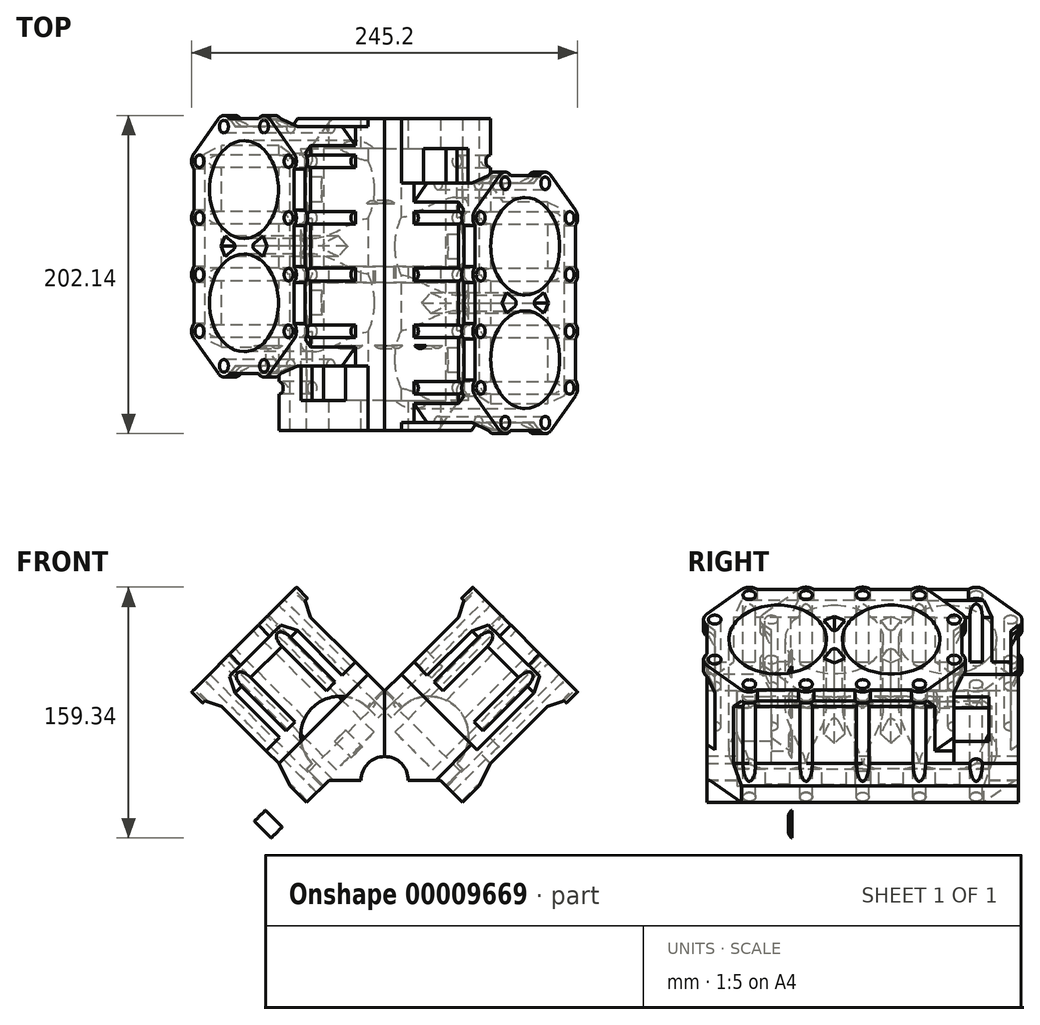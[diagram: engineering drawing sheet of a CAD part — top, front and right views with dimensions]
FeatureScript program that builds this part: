
annotation { "Feature Type Name" : "Feature", "Feature Type Description" : "" }
export const myFeature = defineFeature(function(context is Context, id is Id, definition is map)
    precondition{}
    {
        {
            var Q0;
            Q0=qCreatedBy(makeId("Front.planeOp"),FACE);
            var sketch = newSketch(context, id + "F0", { "sketchPlane" : qUnion([Q0]), "disableImprinting" : false});
            skLineSegment(sketch, "E0", {"start": v(0, 0) * mm, "end": v(-89.32, 89.32) * mm, "construction": true});
            skLineSegment(sketch, "E1", {"start": v(-89.32, 89.32) * mm, "end": v(-61.03, 117.6) * mm});
            skLineSegment(sketch, "E2", {"start": v(-89.32, 89.32) * mm, "end": v(-117.6, 61.03) * mm});
            skArc(sketch, "E3", {"start": v(-10.6, 45.96) * mm, "mid": v(-45.96, 45.96) * mm, "end": v(-45.96, 10.6) * mm});
            skLineSegment(sketch, "E4", {"start": v(0, 15) * mm, "end": v(0, 56.57) * mm});
            skArc(sketch, "E5", {"start": v(0, 15) * mm, "mid": v(-10.6, 10.6) * mm, "end": v(-15, 0) * mm});
            skLineSegment(sketch, "E6", {"start": v(-28.28, 28.28) * mm, "end": v(-10.6, 10.6) * mm});
            skLineSegment(sketch, "E7", {"start": v(0, 56.57) * mm, "end": v(-56.57, 0) * mm});
            skLineSegment(sketch, "E8", {"start": v(-15, 0) * mm, "end": v(-35.36, 0) * mm});
            skLineSegment(sketch, "E9", {"start": v(-56.57, 0) * mm, "end": v(-56.57, 0) * mm});
            skPoint(sketch, "E10", {"position": v(-56.57, 0) * mm});
            skLineSegment(sketch, "E11", {"start": v(-49.5, 7.07) * mm, "end": v(-38.9, -3.54) * mm});
            skLineSegment(sketch, "E12", {"start": v(-48.08, 5.66) * mm, "end": v(-5.61, 48.04) * mm});
            skLineSegment(sketch, "E13", {"start": v(-35.36, 0) * mm, "end": v(-49.5, -14.14) * mm});
            skLineSegment(sketch, "E14", {"start": v(-49.5, -14.14) * mm, "end": v(-60.1, -3.54) * mm});
            skLineSegment(sketch, "E15", {"start": v(-60.1, -3.54) * mm, "end": v(-56.57, 0) * mm});
            skLineSegment(sketch, "E16", {"start": v(-60.1, -3.54) * mm, "end": v(-67.18, 10.6) * mm});
            skLineSegment(sketch, "E17", {"start": v(-7.07, 49.5) * mm, "end": v(-5.61, 48.04) * mm});
            skLineSegment(sketch, "E18", {"start": v(-117.6, 61.03) * mm, "end": v(-121.14, 57.5) * mm});
            skLineSegment(sketch, "E19", {"start": v(-121.14, 57.5) * mm, "end": v(-114.07, 50.43) * mm});
            skLineSegment(sketch, "E20", {"start": v(-114.07, 50.43) * mm, "end": v(-103.46, 46.89) * mm});
            skLineSegment(sketch, "E21", {"start": v(-67.18, 10.6) * mm, "end": v(-103.46, 46.89) * mm});
            skLineSegment(sketch, "E22", {"start": v(-61.03, 117.6) * mm, "end": v(-57.5, 121.14) * mm});
            skLineSegment(sketch, "E23", {"start": v(-57.5, 121.14) * mm, "end": v(-50.43, 114.07) * mm});
            skLineSegment(sketch, "E24", {"start": v(-50.43, 114.07) * mm, "end": v(-46.89, 103.46) * mm});
            skLineSegment(sketch, "E25", {"start": v(-46.89, 103.46) * mm, "end": v(0, 56.57) * mm});
            skSolve(sketch);
        }
        {
            var Q0;
            Q0=makeQuery(id+"F0.imprint","IMPRINT",FACE,{"disambiguationData":[TD([[makeQuery(id+"F0.imprint","IMPRINT",EDGE,{"derivedFrom":sQuery(id+"F0.wireOp",EDGE,"E1")}),-1.0]])]});
            var Q1;
            {var subQ6=sQuery(id+"F0.wireOp",EDGE,"7077ad60-6c45-4a02-82f9-83b4f3b2e26d");Q1=makeQuery(id+"F0.imprint","IMPRINT",FACE,{"disambiguationData":[TD([[makeQuery(id+"F0.imprint","IMPRINT",EDGE,{"derivedFrom":subQ6}),1.0]])]});}
            var Q2;
            {var subQ5=sQuery(id+"F0.wireOp",EDGE,"00a5af6f-d9c4-4420-bd82-b76ba807b053");Q2=makeQuery(id+"F0.imprint","IMPRINT",FACE,{"disambiguationData":[TD([[makeQuery(id+"F0.imprint","IMPRINT",EDGE,{"derivedFrom":subQ5}),1.0]])]});}
            var Q3;
            {var subQ1=sQuery(id+"F0.wireOp",EDGE,"63562ab9-0a50-4102-b09f-f67702f7469f");Q3=makeQuery(id+"F0.imprint","IMPRINT",FACE,{"disambiguationData":[TD([[makeQuery(id+"F0.imprint","IMPRINT",EDGE,{"derivedFrom":subQ1}),1.0]])]});}
            var Q4;
            {var subQ3=sQuery(id+"F0.wireOp",EDGE,"E4");Q4=makeQuery(id+"F0.imprint","IMPRINT",FACE,{"disambiguationData":[TD([[makeQuery(id+"F0.imprint","IMPRINT",EDGE,{"derivedFrom":subQ3}),1.0]])]});}
            var Q5;
            Q5=makeQuery(id+"F0.imprint","IMPRINT",FACE,{"disambiguationData":[TD([[makeQuery(id+"F0.imprint","IMPRINT",EDGE,{"derivedFrom":sQuery(id+"F0.wireOp",EDGE,"61e63e8b-020c-431c-80ea-b96c9f9e3d8e")}),-1.0]])]});
            var Q6;
            {var subQ1=sQuery(id+"F0.wireOp",EDGE,"d73f1ee5-fcce-4fad-9c2f-5dffc275b150");Q6=makeQuery(id+"F0.imprint","IMPRINT",FACE,{"disambiguationData":[TD([[makeQuery(id+"F0.imprint","IMPRINT",EDGE,{"derivedFrom":subQ1}),-1.0]])]});}
            var Q7;
            {var subQ2=sQuery(id+"F0.wireOp",EDGE,"E3");Q7=makeQuery(id+"F0.imprint","IMPRINT",FACE,{"disambiguationData":[TD([[makeQuery(id+"F0.imprint","IMPRINT",EDGE,{"derivedFrom":subQ2}),1.0]])]});}
            var Q8;
            {var subQ0=sQuery(id+"F0.wireOp",EDGE,"E7");var subQ4=sQuery(id+"F0.wireOp",EDGE,"E6");var subQ5=makeQuery(id+"F0.imprint","INTERSECT",VERTEX,{"derivedFrom":[subQ4,subQ0]});Q8=makeQuery(id+"F0.imprint","IMPRINT",FACE,{"disambiguationData":[TD([[makeQuery(id+"F0.imprint","IMPRINT",EDGE,{"disambiguationData":[TD([[subQ5,-1.0]])],"derivedFrom":subQ4}),-1.0]])]});}
            var Q9;
            {var subQ0=sQuery(id+"F0.wireOp",EDGE,"E7");var subQ4=sQuery(id+"F0.wireOp",EDGE,"E6");var subQ6=makeQuery(id+"F0.imprint","INTERSECT",VERTEX,{"derivedFrom":[subQ4,subQ0]});Q9=makeQuery(id+"F0.imprint","IMPRINT",FACE,{"disambiguationData":[TD([[makeQuery(id+"F0.imprint","IMPRINT",EDGE,{"disambiguationData":[TD([[subQ6,-1.0]])],"derivedFrom":subQ4}),1.0]])]});}
            var Q10;
            {var subQ1=sQuery(id+"F0.wireOp",EDGE,"d5e2b67f-3f92-4c55-8c7c-6b2c5aceb9cd");Q10=makeQuery(id+"F0.imprint","IMPRINT",FACE,{"disambiguationData":[TD([[makeQuery(id+"F0.imprint","IMPRINT",EDGE,{"derivedFrom":subQ1}),-1.0]])]});}
            var Q11;
            {var subQ3=sQuery(id+"F0.wireOp",EDGE,"E8");Q11=makeQuery(id+"F0.imprint","IMPRINT",FACE,{"disambiguationData":[TD([[makeQuery(id+"F0.imprint","IMPRINT",EDGE,{"derivedFrom":subQ3}),-1.0]])]});}
            var Q12;
            {var subQ1=sQuery(id+"F0.wireOp",EDGE,"7da52aa7-5538-4868-8c85-49046fa19762");Q12=makeQuery(id+"F0.imprint","IMPRINT",FACE,{"disambiguationData":[TD([[makeQuery(id+"F0.imprint","IMPRINT",EDGE,{"derivedFrom":subQ1}),1.0]])]});}
            var Q13;
            {var subQ1=sQuery(id+"F0.wireOp",EDGE,"E15");Q13=makeQuery(id+"F0.imprint","IMPRINT",FACE,{"disambiguationData":[TD([[makeQuery(id+"F0.imprint","IMPRINT",EDGE,{"derivedFrom":subQ1}),1.0]])]});}
            var Q14;
            {var subQ0=sQuery(id+"F0.wireOp",EDGE,"E14");Q14=makeQuery(id+"F0.imprint","IMPRINT",FACE,{"disambiguationData":[TD([[makeQuery(id+"F0.imprint","IMPRINT",EDGE,{"derivedFrom":subQ0}),-1.0]])]});}
            extrude(context, id + "F1", {"entities" : qUnion([Q0, Q1, Q2, Q3, Q4, Q5, Q6, Q7, Q8, Q9, Q10, Q11, Q12, Q13, Q14]), "depth" : 198 * mm, "symmetric" : true});
        }
        {
            var Q0;
            {var subQ3=sQuery(id+"F0.wireOp",EDGE,"E4");Q0=makeQuery(id+"F0.imprint","IMPRINT",FACE,{"disambiguationData":[TD([[makeQuery(id+"F0.imprint","IMPRINT",EDGE,{"derivedFrom":subQ3}),1.0]])]});}
            var Q1;
            {var subQ0=sQuery(id+"F0.wireOp",EDGE,"E7");var subQ1=sQuery(id+"F0.wireOp",EDGE,"E6");var subQ2=makeQuery(id+"F0.imprint","INTERSECT",VERTEX,{"derivedFrom":[subQ1,subQ0]});Q1=makeQuery(id+"F0.imprint","IMPRINT",FACE,{"disambiguationData":[TD([[makeQuery(id+"F0.imprint","IMPRINT",EDGE,{"disambiguationData":[TD([[subQ2,-1.0]])],"derivedFrom":subQ1}),1.0]])]});}
            var Q2;
            {var subQ0=sQuery(id+"F0.wireOp",EDGE,"E7");var subQ4=sQuery(id+"F0.wireOp",EDGE,"E6");var subQ6=makeQuery(id+"F0.imprint","INTERSECT",VERTEX,{"derivedFrom":[subQ4,subQ0]});Q2=makeQuery(id+"F0.imprint","IMPRINT",FACE,{"disambiguationData":[TD([[makeQuery(id+"F0.imprint","IMPRINT",EDGE,{"disambiguationData":[TD([[subQ6,-1.0]])],"derivedFrom":subQ4}),-1.0]])]});}
            var Q3;
            {var subQ2=sQuery(id+"F0.wireOp",EDGE,"E3");Q3=makeQuery(id+"F0.imprint","IMPRINT",FACE,{"disambiguationData":[TD([[makeQuery(id+"F0.imprint","IMPRINT",EDGE,{"derivedFrom":subQ2}),1.0]])]});}
            var Q4;
            {var subQ2=sQuery(id+"F0.wireOp",EDGE,"E8");Q4=makeQuery(id+"F0.imprint","IMPRINT",FACE,{"disambiguationData":[TD([[makeQuery(id+"F0.imprint","IMPRINT",EDGE,{"derivedFrom":subQ2}),-1.0]])]});}
            extrude(context, id + "F2", {"entities" : qUnion([Q0, Q1, Q2, Q3, Q4]), "operationType" : NewBodyOperationType.REMOVE, "oppositeDirection" : true, "depth" : 160 * mm, "symmetric" : true});
        }
        {
            var Q0;
            Q0=makeQuery(id+"F1.opExtrude","SWEPT_FACE",FACE,{"disambiguationData":[OSD([sQuery(id+"F0.wireOp",EDGE,"E1"),sQuery(id+"F0.wireOp",EDGE,"E2")])]});
            var sketch = newSketch(context, id + "F3", { "sketchPlane" : qUnion([Q0])});
            skArc(sketch, "E26", {"start": v(-20.17, 9.4) * mm, "mid": v(-18, 8.15) * mm, "end": v(-15.83, 9.4) * mm});
            skLineSegment(sketch, "E27", {"start": v(-20.17, 9.4) * mm, "end": v(-24.56, 17) * mm});
            skLineSegment(sketch, "E28", {"start": v(-15.83, 9.4) * mm, "end": v(-11.44, 17) * mm});
            skLineSegment(sketch, "E29", {"start": v(-11.44, -17) * mm, "end": v(-15.83, -9.4) * mm});
            skLineSegment(sketch, "E30", {"start": v(-20.17, -9.4) * mm, "end": v(-24.56, -17) * mm});
            skArc(sketch, "E31", {"start": v(-15.83, -9.4) * mm, "mid": v(-18, -8.15) * mm, "end": v(-20.17, -9.4) * mm});
            skLineSegment(sketch, "E32", {"start": v(-11.44, 17) * mm, "end": v(-18, 20.78) * mm});
            skLineSegment(sketch, "E33", {"start": v(-18, 20.78) * mm, "end": v(-24.56, 17) * mm});
            skLineSegment(sketch, "E34", {"start": v(-24.56, -17) * mm, "end": v(-18, -20.78) * mm});
            skLineSegment(sketch, "E35", {"start": v(-18, -20.78) * mm, "end": v(-11.44, -17) * mm});
            skCircle(sketch, "E36", {"center": v(-54, 0) * mm, "radius": 31 * mm});
            skCircle(sketch, "E37", {"center": v(18, 0) * mm, "radius": 31 * mm});
            skLineSegment(sketch, "E38", {"start": v(18, 0) * mm, "end": v(-11.44, 17) * mm, "construction": true});
            skLineSegment(sketch, "E39", {"start": v(-11.44, -17) * mm, "end": v(18, 0) * mm, "construction": true});
            skLineSegment(sketch, "E40", {"start": v(-18, -20.78) * mm, "end": v(-18, 20.78) * mm, "construction": true});
            skCircle(sketch, "E41", {"center": v(-72, -40) * mm, "radius": 4 * mm});
            skCircle(sketch, "E42", {"center": v(-36, -40) * mm, "radius": 4 * mm});
            skCircle(sketch, "E43", {"center": v(0, -40) * mm, "radius": 4 * mm});
            skCircle(sketch, "E44", {"center": v(36, -40.01) * mm, "radius": 4 * mm});
            skCircle(sketch, "E45", {"center": v(36, 40.01) * mm, "radius": 4 * mm});
            skCircle(sketch, "E46", {"center": v(0, 40) * mm, "radius": 4 * mm});
            skCircle(sketch, "E47", {"center": v(-36, 40) * mm, "radius": 4 * mm});
            skCircle(sketch, "E48", {"center": v(-72, 40) * mm, "radius": 4 * mm});
            skCircle(sketch, "E49", {"center": v(-94, 18) * mm, "radius": 4 * mm});
            skCircle(sketch, "E50", {"center": v(-94, -18) * mm, "radius": 4 * mm});
            skCircle(sketch, "E51", {"center": v(58, 18) * mm, "radius": 4 * mm});
            skCircle(sketch, "E52", {"center": v(58, -18) * mm, "radius": 4 * mm});
            skCircle(sketch, "E53", {"center": v(72, -40) * mm, "radius": 4 * mm});
            skSolve(sketch);
        }
        {
            var Q0;
            {var subQ1=sQuery(id+"F3.wireOp",EDGE,"E37");var subQ3=sQuery(id+"F3.wireOp",EDGE,"ba8a5dc3-78c3-42ff-b71d-fa66224fb622");var subQ5=makeQuery(id+"F3.imprint","INTERSECT",VERTEX,{"derivedFrom":[subQ1,subQ3]});Q0=makeQuery(id+"F3.imprint","IMPRINT",FACE,{"disambiguationData":[TD([[makeQuery(id+"F3.imprint","IMPRINT",EDGE,{"disambiguationData":[TD([[subQ5,-1.0]])],"derivedFrom":subQ1}),1.0]])]});}
            var Q1;
            Q1=makeQuery(id+"F3.imprint","IMPRINT",FACE,{"disambiguationData":[TD([[makeQuery(id+"F3.imprint","IMPRINT",EDGE,{"derivedFrom":sQuery(id+"F3.wireOp",EDGE,"E36")}),1.0]])]});
            var Q2;
            Q2=makeQuery(id+"F3.imprint","IMPRINT",FACE,{"disambiguationData":[TD([[makeQuery(id+"F3.imprint","IMPRINT",EDGE,{"derivedFrom":sQuery(id+"F3.wireOp",EDGE,"E37")}),1.0]])]});
            var Q3;
            Q3=makeQuery(id+"F3.imprint","IMPRINT",FACE,{"disambiguationData":[TD([[makeQuery(id+"F3.imprint","IMPRINT",EDGE,{"derivedFrom":sQuery(id+"F3.wireOp",EDGE,"E29")}),1.0]])]});
            var Q4;
            Q4=makeQuery(id+"F3.imprint","IMPRINT",FACE,{"disambiguationData":[TD([[makeQuery(id+"F3.imprint","IMPRINT",EDGE,{"derivedFrom":sQuery(id+"F3.wireOp",EDGE,"E26")}),1.0]])]});
            extrude(context, id + "F4", {"entities" : qUnion([Q0, Q1, Q2, Q3, Q4]), "operationType" : NewBodyOperationType.REMOVE, "flatOperationType" : FlatOperationType.REMOVE, "oppositeDirection" : true, "depth" : 100 * mm, "offsetDistance" : 25 * mm, "domain" : OperationDomain.MODEL});
        }
        {
            var Q0;
            {var subQ0=sQuery(id+"F0.wireOp",EDGE,"E13");Q0=makeQuery(id+"F7.boolean.opBoolean","MERGE",FACE,{"derivedFrom":[makeQuery(id+"F1.opExtrude","SWEPT_FACE",FACE,{"disambiguationData":[OSD([subQ0])]}),makeQuery(id+"F7.opExtrude","SWEPT_FACE",FACE,{"disambiguationData":[OSD([subQ0])]})]});}
            var sketch = newSketch(context, id + "F5", { "sketchPlane" : qUnion([Q0])});
            skArc(sketch, "E54", {"start": v(-45, -66.95) * mm, "mid": v(-47.07, -71.95) * mm, "end": v(-45, -76.95) * mm});
            skArc(sketch, "E55", {"start": v(-45, -31) * mm, "mid": v(-47.07, -36) * mm, "end": v(-45, -41) * mm});
            skArc(sketch, "E56", {"start": v(-45, 5) * mm, "mid": v(-47.07, 0) * mm, "end": v(-45, -5) * mm});
            skArc(sketch, "E57", {"start": v(-45, 41) * mm, "mid": v(-47.07, 36) * mm, "end": v(-45, 31) * mm});
            skArc(sketch, "E58", {"start": v(-45, 77) * mm, "mid": v(-47.07, 72) * mm, "end": v(-45, 67) * mm});
            skLineSegment(sketch, "E59", {"start": v(-45, -76.95) * mm, "end": v(-45, -66.95) * mm});
            skLineSegment(sketch, "E60", {"start": v(-45, -41) * mm, "end": v(-45, -31) * mm});
            skLineSegment(sketch, "E61", {"start": v(-45, -5) * mm, "end": v(-45, 5) * mm});
            skLineSegment(sketch, "E62", {"start": v(-45, 67) * mm, "end": v(-45, 77) * mm});
            skLineSegment(sketch, "E63", {"start": v(-45, 41) * mm, "end": v(-45, 31) * mm});
            skSolve(sketch);
        }
        {
            var Q0;
            Q0=makeQuery(id+"F5.imprint","IMPRINT",FACE,{"disambiguationData":[TD([[makeQuery(id+"F5.imprint","IMPRINT",EDGE,{"derivedFrom":sQuery(id+"F5.wireOp",EDGE,"E54")}),1.0]])]});
            var Q1;
            Q1=makeQuery(id+"F5.imprint","IMPRINT",FACE,{"disambiguationData":[TD([[makeQuery(id+"F5.imprint","IMPRINT",EDGE,{"derivedFrom":sQuery(id+"F5.wireOp",EDGE,"E55")}),1.0]])]});
            var Q2;
            Q2=makeQuery(id+"F5.imprint","IMPRINT",FACE,{"disambiguationData":[TD([[makeQuery(id+"F5.imprint","IMPRINT",EDGE,{"derivedFrom":sQuery(id+"F5.wireOp",EDGE,"E56")}),1.0]])]});
            var Q3;
            Q3=makeQuery(id+"F5.imprint","IMPRINT",FACE,{"disambiguationData":[TD([[makeQuery(id+"F5.imprint","IMPRINT",EDGE,{"derivedFrom":sQuery(id+"F5.wireOp",EDGE,"E57")}),1.0]])]});
            var Q4;
            Q4=makeQuery(id+"F5.imprint","IMPRINT",FACE,{"disambiguationData":[TD([[makeQuery(id+"F5.imprint","IMPRINT",EDGE,{"derivedFrom":sQuery(id+"F5.wireOp",EDGE,"E58")}),1.0]])]});
            extrude(context, id + "F6", {"entities" : qUnion([Q0, Q1, Q2, Q3, Q4]), "operationType" : NewBodyOperationType.ADD, "oppositeDirection" : true, "depth" : 15 * mm});
        }
        {
            var Q0;
            {var subQ3=sQuery(id+"F0.wireOp",EDGE,"E4");Q0=makeQuery(id+"F0.imprint","IMPRINT",FACE,{"disambiguationData":[TD([[makeQuery(id+"F0.imprint","IMPRINT",EDGE,{"derivedFrom":subQ3}),1.0]])]});}
            var Q1;
            {var subQ3=sQuery(id+"F0.wireOp",EDGE,"E8");Q1=makeQuery(id+"F0.imprint","IMPRINT",FACE,{"disambiguationData":[TD([[makeQuery(id+"F0.imprint","IMPRINT",EDGE,{"derivedFrom":subQ3}),-1.0]])]});}
            var Q2;
            {var subQ1=sQuery(id+"F0.wireOp",EDGE,"7da52aa7-5538-4868-8c85-49046fa19762");Q2=makeQuery(id+"F0.imprint","IMPRINT",FACE,{"disambiguationData":[TD([[makeQuery(id+"F0.imprint","IMPRINT",EDGE,{"derivedFrom":subQ1}),1.0]])]});}
            extrude(context, id + "F7", {"entities" : qUnion([Q0, Q1, Q2]), "operationType" : NewBodyOperationType.ADD, "depth" : 10 * mm, "symmetric" : true});
        }
        {
            var Q0;
            Q0=makeQuery(id+"F3.imprint","IMPRINT",FACE,{"disambiguationData":[TD([[makeQuery(id+"F3.imprint","IMPRINT",EDGE,{"derivedFrom":sQuery(id+"F3.wireOp",EDGE,"E41")}),1.0]])]});
            var Q1;
            Q1=makeQuery(id+"F3.imprint","IMPRINT",FACE,{"disambiguationData":[TD([[makeQuery(id+"F3.imprint","IMPRINT",EDGE,{"derivedFrom":sQuery(id+"F3.wireOp",EDGE,"E42")}),1.0]])]});
            var Q2;
            Q2=makeQuery(id+"F3.imprint","IMPRINT",FACE,{"disambiguationData":[TD([[makeQuery(id+"F3.imprint","IMPRINT",EDGE,{"derivedFrom":sQuery(id+"F3.wireOp",EDGE,"E43")}),1.0]])]});
            var Q3;
            Q3=makeQuery(id+"F3.imprint","IMPRINT",FACE,{"disambiguationData":[TD([[makeQuery(id+"F3.imprint","IMPRINT",EDGE,{"derivedFrom":sQuery(id+"F3.wireOp",EDGE,"E44")}),1.0]])]});
            var Q4;
            Q4=makeQuery(id+"F3.imprint","IMPRINT",FACE,{"disambiguationData":[TD([[makeQuery(id+"F3.imprint","IMPRINT",EDGE,{"derivedFrom":sQuery(id+"F3.wireOp",EDGE,"E53")}),1.0]])]});
            extrude(context, id + "F8", {"entities" : qUnion([Q0, Q1, Q2, Q3, Q4]), "operationType" : NewBodyOperationType.REMOVE, "oppositeDirection" : true, "depth" : 110 * mm});
        }
        {
            var Q0;
            Q0=makeQuery(id+"F1.opExtrude","CAP_FACE",FACE,{"disambiguationData":[OSD([sQuery(id+"F0.wireOp",EDGE,"E1"),sQuery(id+"F0.wireOp",EDGE,"E2"),sQuery(id+"F0.wireOp",EDGE,"E4"),sQuery(id+"F0.wireOp",EDGE,"E5"),sQuery(id+"F0.wireOp",EDGE,"E8"),sQuery(id+"F0.wireOp",EDGE,"E13"),sQuery(id+"F0.wireOp",EDGE,"E14"),sQuery(id+"F0.wireOp",EDGE,"E16"),sQuery(id+"F0.wireOp",EDGE,"E18"),sQuery(id+"F0.wireOp",EDGE,"E19"),sQuery(id+"F0.wireOp",EDGE,"E20"),sQuery(id+"F0.wireOp",EDGE,"E21"),sQuery(id+"F0.wireOp",EDGE,"E22"),sQuery(id+"F0.wireOp",EDGE,"E23"),sQuery(id+"F0.wireOp",EDGE,"E24"),sQuery(id+"F0.wireOp",EDGE,"E25")])],"isStart":true});
            var sketch = newSketch(context, id + "F9", { "sketchPlane" : qUnion([Q0])});
            skLineSegment(sketch, "E64", {"start": v(50.43, 114.07) * mm, "end": v(114.07, 50.43) * mm});
            skLineSegment(sketch, "E65", {"start": v(0, 56.57) * mm, "end": v(60.1, -3.54) * mm});
            skLineSegment(sketch, "E66", {"start": v(67.18, 10.6) * mm, "end": v(10.6, 67.18) * mm});
            skLineSegment(sketch, "E67", {"start": v(10.6, 67.18) * mm, "end": v(46.89, 103.46) * mm});
            skLineSegment(sketch, "E68", {"start": v(46.89, 103.46) * mm, "end": v(103.46, 46.89) * mm});
            skSolve(sketch);
        }
        {
            var Q0;
            Q0=makeQuery(id+"F3.imprint","IMPRINT",FACE,{"disambiguationData":[TD([[makeQuery(id+"F3.imprint","IMPRINT",EDGE,{"derivedFrom":sQuery(id+"F3.wireOp",EDGE,"E50")}),1.0]])]});
            var Q1;
            Q1=makeQuery(id+"F3.imprint","IMPRINT",FACE,{"disambiguationData":[TD([[makeQuery(id+"F3.imprint","IMPRINT",EDGE,{"derivedFrom":sQuery(id+"F3.wireOp",EDGE,"E49")}),1.0]])]});
            var Q2;
            Q2=makeQuery(id+"F3.imprint","IMPRINT",FACE,{"disambiguationData":[TD([[makeQuery(id+"F3.imprint","IMPRINT",EDGE,{"derivedFrom":sQuery(id+"F3.wireOp",EDGE,"E48")}),1.0]])]});
            var Q3;
            Q3=makeQuery(id+"F3.imprint","IMPRINT",FACE,{"disambiguationData":[TD([[makeQuery(id+"F3.imprint","IMPRINT",EDGE,{"derivedFrom":sQuery(id+"F3.wireOp",EDGE,"E47")}),1.0]])]});
            var Q4;
            Q4=makeQuery(id+"F3.imprint","IMPRINT",FACE,{"disambiguationData":[TD([[makeQuery(id+"F3.imprint","IMPRINT",EDGE,{"derivedFrom":sQuery(id+"F3.wireOp",EDGE,"E46")}),1.0]])]});
            var Q5;
            Q5=makeQuery(id+"F3.imprint","IMPRINT",FACE,{"disambiguationData":[TD([[makeQuery(id+"F3.imprint","IMPRINT",EDGE,{"derivedFrom":sQuery(id+"F3.wireOp",EDGE,"E45")}),1.0]])]});
            var Q6;
            Q6=makeQuery(id+"F3.imprint","IMPRINT",FACE,{"disambiguationData":[TD([[makeQuery(id+"F3.imprint","IMPRINT",EDGE,{"derivedFrom":sQuery(id+"F3.wireOp",EDGE,"E51")}),1.0]])]});
            var Q7;
            Q7=makeQuery(id+"F3.imprint","IMPRINT",FACE,{"disambiguationData":[TD([[makeQuery(id+"F3.imprint","IMPRINT",EDGE,{"derivedFrom":sQuery(id+"F3.wireOp",EDGE,"E52")}),1.0]])]});
            extrude(context, id + "F10", {"entities" : qUnion([Q0, Q1, Q2, Q3, Q4, Q5, Q6, Q7]), "operationType" : NewBodyOperationType.REMOVE, "oppositeDirection" : true, "depth" : 60 * mm});
        }
        {
            var Q0;
            Q0=makeQuery(id+"F9.imprint","IMPRINT",FACE,{"disambiguationData":[TD([[makeQuery(id+"F9.imprint","IMPRINT",EDGE,{"derivedFrom":sQuery(id+"F9.wireOp",EDGE,"E66")}),-1.0]])]});
            extrude(context, id + "F11", {"entities" : qUnion([Q0]), "operationType" : NewBodyOperationType.REMOVE, "oppositeDirection" : true, "depth" : 5 * mm});
        }
        {
            var Q0;
            Q0=makeQuery(id+"F1.opExtrude","CAP_FACE",FACE,{"disambiguationData":[OSD([sQuery(id+"F0.wireOp",EDGE,"E1"),sQuery(id+"F0.wireOp",EDGE,"E2"),sQuery(id+"F0.wireOp",EDGE,"E4"),sQuery(id+"F0.wireOp",EDGE,"E5"),sQuery(id+"F0.wireOp",EDGE,"E8"),sQuery(id+"F0.wireOp",EDGE,"E13"),sQuery(id+"F0.wireOp",EDGE,"E14"),sQuery(id+"F0.wireOp",EDGE,"E16"),sQuery(id+"F0.wireOp",EDGE,"E18"),sQuery(id+"F0.wireOp",EDGE,"E19"),sQuery(id+"F0.wireOp",EDGE,"E20"),sQuery(id+"F0.wireOp",EDGE,"E21"),sQuery(id+"F0.wireOp",EDGE,"E22"),sQuery(id+"F0.wireOp",EDGE,"E23"),sQuery(id+"F0.wireOp",EDGE,"E24"),sQuery(id+"F0.wireOp",EDGE,"E25")])],"isStart":false});
            var sketch = newSketch(context, id + "F12", { "sketchPlane" : qUnion([Q0])});
            skLineSegment(sketch, "E69", {"start": v(-60.1, -3.54) * mm, "end": v(0, 56.57) * mm});
            skLineSegment(sketch, "E70", {"start": v(-103.46, 46.89) * mm, "end": v(-46.89, 103.46) * mm});
            skLineSegment(sketch, "E71", {"start": v(-50.43, 114.07) * mm, "end": v(-114.07, 50.43) * mm});
            skLineSegment(sketch, "E72", {"start": v(-67.18, 10.6) * mm, "end": v(-10.6, 67.18) * mm});
            skSolve(sketch);
        }
        {
            var Q0;
            Q0 = qSketchRegion(id + "F12", true);
            var Q1;
            {var subQ2=sQuery(id+"F12.wireOp",EDGE,"E70");Q1=makeQuery(id+"F12.imprint","IMPRINT",FACE,{"disambiguationData":[TD([[makeQuery(id+"F12.imprint","IMPRINT",EDGE,{"derivedFrom":subQ2}),-1.0]])]});}
            extrude(context, id + "F13", {"entities" : qUnion([Q0, Q1]), "operationType" : NewBodyOperationType.REMOVE, "oppositeDirection" : true, "depth" : 41 * mm});
        }
        {
            var Q0;
            {var subQ0=sQuery(id+"F0.wireOp",EDGE,"E1");var subQ1=sQuery(id+"F0.wireOp",EDGE,"E2");var subQ2=sQuery(id+"F0.wireOp",EDGE,"E18");var subQ3=sQuery(id+"F0.wireOp",EDGE,"E19");var subQ4=sQuery(id+"F0.wireOp",EDGE,"E20");var subQ5=sQuery(id+"F0.wireOp",EDGE,"E22");var subQ6=sQuery(id+"F0.wireOp",EDGE,"E23");var subQ7=sQuery(id+"F0.wireOp",EDGE,"E24");Q0=makeQuery(id+"F13.boolean.opBoolean","SPLIT",FACE,{"disambiguationData":[TD([makeQuery(id+"F1.opExtrude","SWEPT_FACE",FACE,{"disambiguationData":[OSD([subQ3])]})])],"derivedFrom":makeQuery(id+"F1.opExtrude","CAP_FACE",FACE,{"disambiguationData":[OSD([subQ0,subQ1,sQuery(id+"F0.wireOp",EDGE,"E4"),sQuery(id+"F0.wireOp",EDGE,"E5"),sQuery(id+"F0.wireOp",EDGE,"E8"),sQuery(id+"F0.wireOp",EDGE,"E13"),sQuery(id+"F0.wireOp",EDGE,"E14"),sQuery(id+"F0.wireOp",EDGE,"E16"),subQ2,subQ3,subQ4,sQuery(id+"F0.wireOp",EDGE,"E21"),subQ5,subQ6,subQ7,sQuery(id+"F0.wireOp",EDGE,"E25")])],"isStart":false})});}
            extrude(context, id + "F14", {"entities" : qUnion([Q0]), "operationType" : NewBodyOperationType.REMOVE, "oppositeDirection" : true, "depth" : 36 * mm});
        }
        {
            var Q0;
            Q0=makeQuery(id+"F3.imprint","IMPRINT",FACE,{"disambiguationData":[TD([[makeQuery(id+"F3.imprint","IMPRINT",EDGE,{"derivedFrom":sQuery(id+"F3.wireOp",EDGE,"E26")}),-1.0]])]});
            var sketch = newSketch(context, id + "F15", { "sketchPlane" : qUnion([Q0])});
            skArc(sketch, "E73", {"start": v(31, -45) * mm, "mid": v(36, -47.08) * mm, "end": v(41, -45) * mm});
            skArc(sketch, "E74", {"start": v(-4.99, -45) * mm, "mid": v(0, -47.06) * mm, "end": v(4.99, -45) * mm});
            skArc(sketch, "E75", {"start": v(-40.99, -45) * mm, "mid": v(-36, -47.06) * mm, "end": v(-31.01, -45) * mm});
            skArc(sketch, "E76", {"start": v(-76.99, -45) * mm, "mid": v(-72, -47.06) * mm, "end": v(-67.01, -45) * mm});
            skArc(sketch, "E77", {"start": v(41, 45) * mm, "mid": v(36, 47.08) * mm, "end": v(31, 45) * mm});
            skArc(sketch, "E78", {"start": v(5, 45) * mm, "mid": v(0, 47.08) * mm, "end": v(-5, 45) * mm});
            skArc(sketch, "E79", {"start": v(-31, 45) * mm, "mid": v(-36, 47.08) * mm, "end": v(-41, 45) * mm});
            skArc(sketch, "E80", {"start": v(-67.01, 45) * mm, "mid": v(-72, 47.06) * mm, "end": v(-76.99, 45) * mm});
            skLineSegment(sketch, "E81", {"start": v(41, 45) * mm, "end": v(-76.99, 45) * mm});
            skLineSegment(sketch, "E82", {"start": v(41, -45) * mm, "end": v(-76.99, -45) * mm});
            skArc(sketch, "E83", {"start": v(63, 13) * mm, "mid": v(65.07, 18) * mm, "end": v(63, 23) * mm});
            skArc(sketch, "E84", {"start": v(63, -23) * mm, "mid": v(65.07, -18) * mm, "end": v(63, -13) * mm});
            skLineSegment(sketch, "E85", {"start": v(63, 23) * mm, "end": v(63, -23) * mm});
            skLineSegment(sketch, "E86", {"start": v(63, -23) * mm, "end": v(41, -45) * mm});
            skLineSegment(sketch, "E87", {"start": v(63, 23) * mm, "end": v(41, 45) * mm});
            skLineSegment(sketch, "E88", {"start": v(63, 23) * mm, "end": v(63, 45.03) * mm});
            skLineSegment(sketch, "E89", {"start": v(63, 45.03) * mm, "end": v(41, 45) * mm});
            skLineSegment(sketch, "E90", {"start": v(41, -45) * mm, "end": v(63, -45) * mm});
            skLineSegment(sketch, "E91", {"start": v(63, -45) * mm, "end": v(63, -23) * mm});
            skArc(sketch, "E92", {"start": v(-99, -13) * mm, "mid": v(-101.07, -18) * mm, "end": v(-99, -23) * mm});
            skArc(sketch, "E93", {"start": v(-99, 23) * mm, "mid": v(-101.07, 18) * mm, "end": v(-99, 13) * mm});
            skLineSegment(sketch, "E94", {"start": v(-99, -23) * mm, "end": v(-99, 23) * mm});
            skLineSegment(sketch, "E95", {"start": v(-76.99, -45) * mm, "end": v(-99, -23) * mm});
            skLineSegment(sketch, "E96", {"start": v(-99, 23) * mm, "end": v(-76.99, 45) * mm});
            skLineSegment(sketch, "E97", {"start": v(-76.99, -45) * mm, "end": v(-99, -45) * mm});
            skLineSegment(sketch, "E98", {"start": v(-99, -45) * mm, "end": v(-99, -23) * mm});
            skLineSegment(sketch, "E99", {"start": v(-99, 23) * mm, "end": v(-99, 45) * mm});
            skLineSegment(sketch, "E100", {"start": v(-76.99, 45) * mm, "end": v(-99, 45) * mm});
            skSolve(sketch);
        }
        {
            var Q0;
            Q0=makeQuery(id+"F14.boolean.opBoolean","COPY",VERTEX,{"derivedFrom":makeQuery(id+"F14.opExtrude","CAP_VERTEX",VERTEX,{"disambiguationData":[OSD([sQuery(id+"F0.wireOp",EDGE,"E19"),sQuery(id+"F0.wireOp",EDGE,"E20")])],"isStart":false})});
            var Q1;
            Q1=makeQuery(id+"F14.boolean.opBoolean","COPY",VERTEX,{"derivedFrom":makeQuery(id+"F14.opExtrude","CAP_VERTEX",VERTEX,{"disambiguationData":[OSD([sQuery(id+"F0.wireOp",EDGE,"E23"),sQuery(id+"F0.wireOp",EDGE,"E24")])],"isStart":false})});
            var Q2;
            Q2=makeQuery(id+"F13.boolean.opBoolean","COPY",VERTEX,{"derivedFrom":makeQuery(id+"F13.opExtrude","CAP_VERTEX",VERTEX,{"disambiguationData":[OSD([sQuery(id+"F0.wireOp",EDGE,"E20"),sQuery(id+"F0.wireOp",EDGE,"E21"),sQuery(id+"F12.wireOp",EDGE,"E70")])],"isStart":false})});
            cPlane(context, id + "F16", {"entities" : qUnion([Q0, Q1, Q2]), "cplaneType" : CPlaneType.THREE_POINT, "offset" : 150 * mm, "width" : 150 * mm, "height" : 150 * mm});
        }
        {
            var Q0;
            Q0=makeQuery(id+"F1.opExtrude","CAP_VERTEX",VERTEX,{"disambiguationData":[OSD([sQuery(id+"F0.wireOp",EDGE,"E23"),sQuery(id+"F0.wireOp",EDGE,"E24")])],"isStart":true});
            var Q1;
            Q1=makeQuery(id+"F1.opExtrude","CAP_VERTEX",VERTEX,{"disambiguationData":[OSD([sQuery(id+"F0.wireOp",EDGE,"E19"),sQuery(id+"F0.wireOp",EDGE,"E20")])],"isStart":true});
            var Q2;
            Q2=makeQuery(id+"F11.boolean.opBoolean","COPY",VERTEX,{"derivedFrom":makeQuery(id+"F11.opExtrude","CAP_VERTEX",VERTEX,{"disambiguationData":[OSD([sQuery(id+"F0.wireOp",EDGE,"E24"),sQuery(id+"F9.wireOp",EDGE,"E67"),sQuery(id+"F9.wireOp",EDGE,"E68")])],"isStart":false})});
            cPlane(context, id + "F17", {"entities" : qUnion([Q0, Q1, Q2]), "cplaneType" : CPlaneType.THREE_POINT, "offset" : 150 * mm, "width" : 150 * mm, "height" : 150 * mm});
        }
        {
            var Q0;
            Q0=makeQuery(id+"F14.boolean.opBoolean","COPY",FACE,{"derivedFrom":makeQuery(id+"F14.opExtrude","CAP_FACE",FACE,{"disambiguationData":[OSD([sQuery(id+"F0.wireOp",EDGE,"E1"),sQuery(id+"F0.wireOp",EDGE,"E2"),sQuery(id+"F0.wireOp",EDGE,"E4"),sQuery(id+"F0.wireOp",EDGE,"E5"),sQuery(id+"F0.wireOp",EDGE,"E8"),sQuery(id+"F0.wireOp",EDGE,"E13"),sQuery(id+"F0.wireOp",EDGE,"E14"),sQuery(id+"F0.wireOp",EDGE,"E16"),sQuery(id+"F0.wireOp",EDGE,"E18"),sQuery(id+"F0.wireOp",EDGE,"E19"),sQuery(id+"F0.wireOp",EDGE,"E20"),sQuery(id+"F0.wireOp",EDGE,"E21"),sQuery(id+"F0.wireOp",EDGE,"E22"),sQuery(id+"F0.wireOp",EDGE,"E23"),sQuery(id+"F0.wireOp",EDGE,"E24"),sQuery(id+"F0.wireOp",EDGE,"E25")])],"isStart":false})});
            var sketch = newSketch(context, id + "F18", { "sketchPlane" : qUnion([Q0])});
            skLineSegment(sketch, "E101", {"start": v(-114.07, 50.43) * mm, "end": v(-50.43, 114.07) * mm});
            skSolve(sketch);
        }
        {
            var Q0;
            {var subQ0=sQuery(id+"F0.wireOp",EDGE,"E1");var subQ1=sQuery(id+"F0.wireOp",EDGE,"E2");var subQ2=sQuery(id+"F0.wireOp",EDGE,"E18");var subQ3=sQuery(id+"F0.wireOp",EDGE,"E19");var subQ4=sQuery(id+"F0.wireOp",EDGE,"E20");var subQ5=sQuery(id+"F0.wireOp",EDGE,"E22");var subQ6=sQuery(id+"F0.wireOp",EDGE,"E23");var subQ7=sQuery(id+"F0.wireOp",EDGE,"E24");Q0=makeQuery(id+"F11.boolean.opBoolean","SPLIT",FACE,{"disambiguationData":[TD([makeQuery(id+"F1.opExtrude","SWEPT_FACE",FACE,{"disambiguationData":[OSD([subQ3])]})])],"derivedFrom":makeQuery(id+"F1.opExtrude","CAP_FACE",FACE,{"disambiguationData":[OSD([subQ0,subQ1,sQuery(id+"F0.wireOp",EDGE,"E4"),sQuery(id+"F0.wireOp",EDGE,"E5"),sQuery(id+"F0.wireOp",EDGE,"E8"),sQuery(id+"F0.wireOp",EDGE,"E13"),sQuery(id+"F0.wireOp",EDGE,"E14"),sQuery(id+"F0.wireOp",EDGE,"E16"),subQ2,subQ3,subQ4,sQuery(id+"F0.wireOp",EDGE,"E21"),subQ5,subQ6,subQ7,sQuery(id+"F0.wireOp",EDGE,"E25")])],"isStart":true})});}
            var sketch = newSketch(context, id + "F19", { "sketchPlane" : qUnion([Q0])});
            skLineSegment(sketch, "E102", {"start": v(50.43, 114.07) * mm, "end": v(114.07, 50.43) * mm});
            skSolve(sketch);
        }
        {
            var Q0;
            Q0=makeQuery(id+"F19.imprint","IMPRINT",FACE,{"disambiguationData":[TD([[makeQuery(id+"F19.imprint","IMPRINT",EDGE,{"derivedFrom":sQuery(id+"F19.wireOp",EDGE,"E102")}),-1.0]])]});
            var Q1;
            Q1=qCreatedBy(id+"F17.planeOp",FACE);
            extrude(context, id + "F20", {"entities" : qUnion([Q0]), "operationType" : NewBodyOperationType.REMOVE, "endBound" : BoundingType.UP_TO_SURFACE, "oppositeDirection" : true, "endBoundEntityFace" : qUnion([Q1]), "depth" : 25 * mm});
        }
        {
            var Q0;
            Q0=makeQuery(id+"F18.imprint","IMPRINT",FACE,{"disambiguationData":[TD([[makeQuery(id+"F18.imprint","IMPRINT",EDGE,{"derivedFrom":sQuery(id+"F18.wireOp",EDGE,"E101")}),-1.0]])]});
            var Q1;
            Q1=qCreatedBy(id+"F16.planeOp",FACE);
            extrude(context, id + "F21", {"entities" : qUnion([Q0]), "operationType" : NewBodyOperationType.REMOVE, "endBound" : BoundingType.UP_TO_SURFACE, "oppositeDirection" : true, "endBoundEntityFace" : qUnion([Q1]), "depth" : 25 * mm});
        }
        {
            var Q0;
            {var subQ1=sQuery(id+"F15.wireOp",EDGE,"E80");Q0=makeQuery(id+"F15.imprint","IMPRINT",FACE,{"disambiguationData":[TD([[makeQuery(id+"F15.imprint","IMPRINT",EDGE,{"derivedFrom":subQ1}),1.0]])]});}
            var Q1;
            {var subQ1=sQuery(id+"F15.wireOp",EDGE,"E76");Q1=makeQuery(id+"F15.imprint","IMPRINT",FACE,{"disambiguationData":[TD([[makeQuery(id+"F15.imprint","IMPRINT",EDGE,{"derivedFrom":subQ1}),1.0]])]});}
            var Q2;
            {var subQ1=sQuery(id+"F15.wireOp",EDGE,"E75");Q2=makeQuery(id+"F15.imprint","IMPRINT",FACE,{"disambiguationData":[TD([[makeQuery(id+"F15.imprint","IMPRINT",EDGE,{"derivedFrom":subQ1}),1.0]])]});}
            var Q3;
            {var subQ1=sQuery(id+"F15.wireOp",EDGE,"E79");Q3=makeQuery(id+"F15.imprint","IMPRINT",FACE,{"disambiguationData":[TD([[makeQuery(id+"F15.imprint","IMPRINT",EDGE,{"derivedFrom":subQ1}),1.0]])]});}
            var Q4;
            {var subQ1=sQuery(id+"F15.wireOp",EDGE,"E78");Q4=makeQuery(id+"F15.imprint","IMPRINT",FACE,{"disambiguationData":[TD([[makeQuery(id+"F15.imprint","IMPRINT",EDGE,{"derivedFrom":subQ1}),1.0]])]});}
            var Q5;
            {var subQ1=sQuery(id+"F15.wireOp",EDGE,"E77");Q5=makeQuery(id+"F15.imprint","IMPRINT",FACE,{"disambiguationData":[TD([[makeQuery(id+"F15.imprint","IMPRINT",EDGE,{"derivedFrom":subQ1}),1.0]])]});}
            var Q6;
            {var subQ1=sQuery(id+"F15.wireOp",EDGE,"E73");Q6=makeQuery(id+"F15.imprint","IMPRINT",FACE,{"disambiguationData":[TD([[makeQuery(id+"F15.imprint","IMPRINT",EDGE,{"derivedFrom":subQ1}),1.0]])]});}
            var Q7;
            {var subQ1=sQuery(id+"F15.wireOp",EDGE,"E74");Q7=makeQuery(id+"F15.imprint","IMPRINT",FACE,{"disambiguationData":[TD([[makeQuery(id+"F15.imprint","IMPRINT",EDGE,{"derivedFrom":subQ1}),1.0]])]});}
            var Q8;
            {var subQ1=sQuery(id+"F15.wireOp",EDGE,"E83");Q8=makeQuery(id+"F15.imprint","IMPRINT",FACE,{"disambiguationData":[TD([[makeQuery(id+"F15.imprint","IMPRINT",EDGE,{"derivedFrom":subQ1}),1.0]])]});}
            var Q9;
            {var subQ1=sQuery(id+"F15.wireOp",EDGE,"E84");Q9=makeQuery(id+"F15.imprint","IMPRINT",FACE,{"disambiguationData":[TD([[makeQuery(id+"F15.imprint","IMPRINT",EDGE,{"derivedFrom":subQ1}),1.0]])]});}
            var Q10;
            {var subQ1=sQuery(id+"F15.wireOp",EDGE,"E92");Q10=makeQuery(id+"F15.imprint","IMPRINT",FACE,{"disambiguationData":[TD([[makeQuery(id+"F15.imprint","IMPRINT",EDGE,{"derivedFrom":subQ1}),1.0]])]});}
            var Q11;
            {var subQ1=sQuery(id+"F15.wireOp",EDGE,"E93");Q11=makeQuery(id+"F15.imprint","IMPRINT",FACE,{"disambiguationData":[TD([[makeQuery(id+"F15.imprint","IMPRINT",EDGE,{"derivedFrom":subQ1}),1.0]])]});}
            extrude(context, id + "F22", {"entities" : qUnion([Q0, Q1, Q2, Q3, Q4, Q5, Q6, Q7, Q8, Q9, Q10, Q11]), "operationType" : NewBodyOperationType.ADD, "oppositeDirection" : true, "depth" : 10 * mm});
        }
        {
            var Q0;
            {var subQ3=sQuery(id+"F15.wireOp",EDGE,"E87");Q0=makeQuery(id+"F15.imprint","IMPRINT",FACE,{"disambiguationData":[TD([[makeQuery(id+"F15.imprint","IMPRINT",EDGE,{"derivedFrom":subQ3}),-1.0]])]});}
            var Q1;
            Q1=makeQuery(id+"F15.imprint","IMPRINT",FACE,{"disambiguationData":[TD([[makeQuery(id+"F15.imprint","IMPRINT",EDGE,{"derivedFrom":sQuery(id+"F15.wireOp",EDGE,"E96")}),1.0]])]});
            var Q2;
            Q2=makeQuery(id+"F15.imprint","IMPRINT",FACE,{"disambiguationData":[TD([[makeQuery(id+"F15.imprint","IMPRINT",EDGE,{"derivedFrom":sQuery(id+"F15.wireOp",EDGE,"E86")}),1.0]])]});
            extrude(context, id + "F23", {"entities" : qUnion([Q0, Q1, Q2]), "operationType" : NewBodyOperationType.REMOVE, "oppositeDirection" : true, "depth" : 60 * mm});
        }
        {
            var Q0;
            Q0=makeQuery(id+"F15.imprint","IMPRINT",FACE,{"disambiguationData":[TD([[makeQuery(id+"F15.imprint","IMPRINT",EDGE,{"derivedFrom":sQuery(id+"F15.wireOp",EDGE,"E95")}),1.0]])]});
            extrude(context, id + "F24", {"entities" : qUnion([Q0]), "operationType" : NewBodyOperationType.REMOVE, "oppositeDirection" : true, "depth" : 125 * mm});
        }
        {
            var Q0;
            {var subQ0=sQuery(id+"F0.wireOp",EDGE,"E13");Q0=makeQuery(id+"F7.boolean.opBoolean","MERGE",FACE,{"derivedFrom":[makeQuery(id+"F6.boolean.opBoolean","MERGE",FACE,{"derivedFrom":[makeQuery(id+"F1.opExtrude","SWEPT_FACE",FACE,{"disambiguationData":[OSD([subQ0])]}),makeQuery(id+"F6.opExtrude","CAP_FACE",FACE,{"disambiguationData":[OSD([sQuery(id+"F5.wireOp",EDGE,"E54"),sQuery(id+"F5.wireOp",EDGE,"E59")])],"isStart":true}),makeQuery(id+"F6.opExtrude","CAP_FACE",FACE,{"disambiguationData":[OSD([sQuery(id+"F5.wireOp",EDGE,"E55"),sQuery(id+"F5.wireOp",EDGE,"E60")])],"isStart":true}),makeQuery(id+"F6.opExtrude","CAP_FACE",FACE,{"disambiguationData":[OSD([sQuery(id+"F5.wireOp",EDGE,"E56"),sQuery(id+"F5.wireOp",EDGE,"E61")])],"isStart":true}),makeQuery(id+"F6.opExtrude","CAP_FACE",FACE,{"disambiguationData":[OSD([sQuery(id+"F5.wireOp",EDGE,"E57"),sQuery(id+"F5.wireOp",EDGE,"E63")])],"isStart":true}),makeQuery(id+"F6.opExtrude","CAP_FACE",FACE,{"disambiguationData":[OSD([sQuery(id+"F5.wireOp",EDGE,"E58"),sQuery(id+"F5.wireOp",EDGE,"E62")])],"isStart":true})]}),makeQuery(id+"F7.opExtrude","SWEPT_FACE",FACE,{"disambiguationData":[OSD([subQ0])]})]});}
            var sketch = newSketch(context, id + "F25", { "sketchPlane" : qUnion([Q0])});
            skLineSegment(sketch, "E103", {"start": v(-45, 77) * mm, "end": v(-23, 99) * mm});
            skLineSegment(sketch, "E104", {"start": v(-23, 99) * mm, "end": v(-45, 99) * mm});
            skLineSegment(sketch, "E105", {"start": v(-45, 99) * mm, "end": v(-45, 77) * mm});
            skSolve(sketch);
        }
        {
            var Q0;
            {var subQ9=sQuery(id+"F25.wireOp",EDGE,"E105");Q0=makeQuery(id+"F25.imprint","IMPRINT",FACE,{"disambiguationData":[TD([[makeQuery(id+"F25.imprint","IMPRINT",EDGE,{"derivedFrom":subQ9}),1.0]])]});}
            var Q1;
            {var subQ5=sQuery(id+"F25.wireOp",EDGE,"E103");var subQ7=sQuery(id+"F25.wireOp",EDGE,"E104");var subQ9=makeQuery(id+"F25.imprint","INTERSECT",VERTEX,{"derivedFrom":[subQ5,subQ7]});Q1=makeQuery(id+"F25.imprint","IMPRINT",FACE,{"disambiguationData":[TD([[makeQuery(id+"F25.imprint","IMPRINT",EDGE,{"disambiguationData":[TD([[subQ9,1.0]])],"derivedFrom":subQ5}),1.0]])]});}
            extrude(context, id + "F26", {"entities" : qUnion([Q0, Q1]), "operationType" : NewBodyOperationType.REMOVE, "oppositeDirection" : true, "depth" : 60 * mm, "symmetric" : true});
        }
        {
            var Q0;
            Q0=makeQuery(id+"F1.opExtrude","SWEPT_BODY",BODY,{"disambiguationData":[OSD([sQuery(id+"F0.wireOp",EDGE,"E1"),sQuery(id+"F0.wireOp",EDGE,"E2"),sQuery(id+"F0.wireOp",EDGE,"E4"),sQuery(id+"F0.wireOp",EDGE,"E5"),sQuery(id+"F0.wireOp",EDGE,"E8"),sQuery(id+"F0.wireOp",EDGE,"E13"),sQuery(id+"F0.wireOp",EDGE,"E14"),sQuery(id+"F0.wireOp",EDGE,"E16"),sQuery(id+"F0.wireOp",EDGE,"E18"),sQuery(id+"F0.wireOp",EDGE,"E19"),sQuery(id+"F0.wireOp",EDGE,"E20"),sQuery(id+"F0.wireOp",EDGE,"E21"),sQuery(id+"F0.wireOp",EDGE,"E22"),sQuery(id+"F0.wireOp",EDGE,"E23"),sQuery(id+"F0.wireOp",EDGE,"E24"),sQuery(id+"F0.wireOp",EDGE,"E25")])]});
            var Q1;
            Q1=sQuery(id+"F0.wireOp",EDGE,"E4");
            transform(context, id + "F27", {"entities" : qUnion([Q0]), "transformType" : TransformType.ROTATION, "transformAxis" : qUnion([Q1]), "angle" : 180 * degree, "makeCopy" : true});
        }
    });
